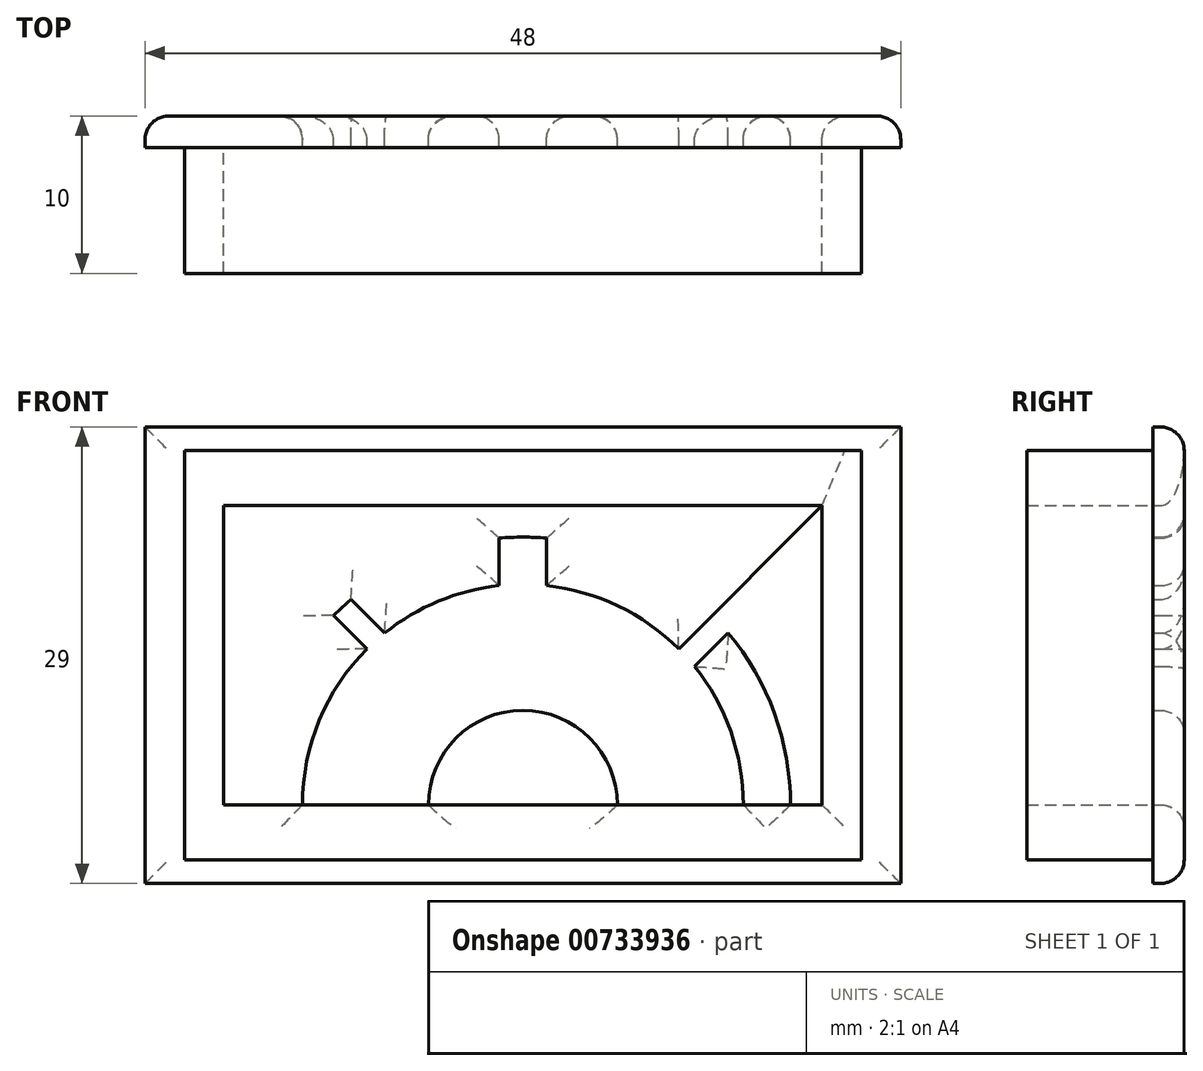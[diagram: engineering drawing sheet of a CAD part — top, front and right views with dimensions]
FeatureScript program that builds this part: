
annotation { "Feature Type Name" : "Feature", "Feature Type Description" : "" }
export const myFeature = defineFeature(function(context is Context, id is Id, definition is map)
    precondition{}
    {
        {
            var Q0;
            Q0=qCreatedBy(makeId("Front.planeOp"),FACE);
            var sketch = newSketch(context, id + "F0", { "sketchPlane" : qUnion([Q0])});
            skLineSegment(sketch, "E0.bottom", {"start": v(0, 0) * mm, "end": v(48, 0) * mm});
            skLineSegment(sketch, "E0.top", {"start": v(0, 29) * mm, "end": v(48, 29) * mm});
            skLineSegment(sketch, "E0.left", {"start": v(0, 0) * mm, "end": v(0, 29) * mm});
            skLineSegment(sketch, "E0.right", {"start": v(48, 0) * mm, "end": v(48, 29) * mm});
            skLineSegment(sketch, "E1.bottom", {"start": v(5, 24) * mm, "end": v(43, 24) * mm});
            skLineSegment(sketch, "E1.top", {"start": v(5, 5) * mm, "end": v(43, 5) * mm});
            skLineSegment(sketch, "E1.left", {"start": v(5, 24) * mm, "end": v(5, 5) * mm});
            skLineSegment(sketch, "E1.right", {"start": v(43, 24) * mm, "end": v(43, 5) * mm});
            skLineSegment(sketch, "E2.bottom", {"start": v(2.5, 27.5) * mm, "end": v(45.5, 27.5) * mm});
            skLineSegment(sketch, "E2.top", {"start": v(2.5, 1.5) * mm, "end": v(45.5, 1.5) * mm});
            skLineSegment(sketch, "E2.left", {"start": v(2.5, 27.5) * mm, "end": v(2.5, 1.5) * mm});
            skLineSegment(sketch, "E2.right", {"start": v(45.5, 27.5) * mm, "end": v(45.5, 1.5) * mm});
            skArc(sketch, "E3", {"start": v(7, 5) * mm, "mid": v(24, 22) * mm, "end": v(41, 5) * mm});
            skArc(sketch, "E4", {"start": v(10, 5) * mm, "mid": v(24, 19) * mm, "end": v(38, 5) * mm});
            skArc(sketch, "E5", {"start": v(18, 5) * mm, "mid": v(24, 11) * mm, "end": v(30, 5) * mm});
            skLineSegment(sketch, "E6", {"start": v(5, 24) * mm, "end": v(19.76, 9.24) * mm});
            skLineSegment(sketch, "E7", {"start": v(43, 24) * mm, "end": v(28.24, 9.24) * mm});
            skLineSegment(sketch, "E8", {"start": v(7.12, 24) * mm, "end": v(21.88, 9.24) * mm});
            skLineSegment(sketch, "E9", {"start": v(5, 21.88) * mm, "end": v(19.9, 6.97) * mm});
            skLineSegment(sketch, "E10", {"start": v(40.88, 24) * mm, "end": v(27.05, 10.17) * mm});
            skLineSegment(sketch, "E11", {"start": v(43, 21.88) * mm, "end": v(29.17, 8.05) * mm});
            skLineSegment(sketch, "E12", {"start": v(22.5, 24) * mm, "end": v(22.5, 10.8) * mm});
            skLineSegment(sketch, "E13", {"start": v(25.5, 24) * mm, "end": v(25.5, 10.8) * mm});
            skSolve(sketch);
        }
        {
            var Q0;
            Q0=makeQuery(id+"F0.imprint","IMPRINT",FACE,{"disambiguationData":[TD([[makeQuery(id+"F0.imprint","IMPRINT",EDGE,{"derivedFrom":sQuery(id+"F0.wireOp",EDGE,"E1.bottom")}),1.0]])]});
            extrude(context, id + "F1", {"entities" : qUnion([Q0]), "depth" : 10 * mm, "offsetDistance" : 25 * mm});
        }
        {
            var Q0;
            {var subQ0=sQuery(id+"F0.wireOp",EDGE,"E12");var subQ1=sQuery(id+"F0.wireOp",EDGE,"E1.bottom");var subQ2=makeQuery(id+"F0.imprint","INTERSECT",VERTEX,{"derivedFrom":[subQ1,subQ0]});Q0=makeQuery(id+"F0.imprint","IMPRINT",FACE,{"disambiguationData":[TD([[makeQuery(id+"F0.imprint","IMPRINT",EDGE,{"disambiguationData":[TD([[subQ2,-1.0]])],"derivedFrom":subQ1}),-1.0]])]});}
            var Q1;
            {var subQ3=sQuery(id+"F0.wireOp",EDGE,"E10");var subQ5=sQuery(id+"F0.wireOp",EDGE,"E3");var subQ6=makeQuery(id+"F0.imprint","INTERSECT",VERTEX,{"derivedFrom":[subQ5,subQ3]});Q1=makeQuery(id+"F0.imprint","IMPRINT",FACE,{"disambiguationData":[TD([[makeQuery(id+"F0.imprint","IMPRINT",EDGE,{"disambiguationData":[TD([[subQ6,-1.0]])],"derivedFrom":subQ5}),1.0]])]});}
            var Q2;
            Q2=makeQuery(id+"F0.imprint","IMPRINT",FACE,{"disambiguationData":[TD([[makeQuery(id+"F0.imprint","IMPRINT",EDGE,{"derivedFrom":sQuery(id+"F0.wireOp",EDGE,"E0.bottom")}),1.0]])]});
            var Q3;
            {var subQ0=sQuery(id+"F0.wireOp",EDGE,"E3");var subQ1=sQuery(id+"F0.wireOp",EDGE,"E1.top");var subQ2=makeQuery(id+"F0.imprint","INTERSECT",VERTEX,{"disambiguationData":[OD(0.0)],"derivedFrom":[subQ1,subQ0]});Q3=makeQuery(id+"F0.imprint","IMPRINT",FACE,{"disambiguationData":[TD([[makeQuery(id+"F0.imprint","IMPRINT",EDGE,{"disambiguationData":[TD([[subQ2,-1.0]])],"derivedFrom":subQ1}),1.0]])]});}
            var Q4;
            {var subQ0=sQuery(id+"F0.wireOp",EDGE,"E3");var subQ1=sQuery(id+"F0.wireOp",EDGE,"E1.top");var subQ2=makeQuery(id+"F0.imprint","INTERSECT",VERTEX,{"disambiguationData":[OD(1.0)],"derivedFrom":[subQ1,subQ0]});Q4=makeQuery(id+"F0.imprint","IMPRINT",FACE,{"disambiguationData":[TD([[makeQuery(id+"F0.imprint","IMPRINT",EDGE,{"disambiguationData":[TD([[subQ2,1.0]])],"derivedFrom":subQ1}),1.0]])]});}
            var Q5;
            {var subQ0=sQuery(id+"F0.wireOp",EDGE,"E9");var subQ1=sQuery(id+"F0.wireOp",EDGE,"E3");var subQ2=makeQuery(id+"F0.imprint","INTERSECT",VERTEX,{"derivedFrom":[subQ1,subQ0]});Q5=makeQuery(id+"F0.imprint","IMPRINT",FACE,{"disambiguationData":[TD([[makeQuery(id+"F0.imprint","IMPRINT",EDGE,{"disambiguationData":[TD([[subQ2,-1.0]])],"derivedFrom":subQ1}),-1.0]])]});}
            var Q6;
            {var subQ0=sQuery(id+"F0.wireOp",EDGE,"E6");var subQ1=sQuery(id+"F0.wireOp",EDGE,"E3");var subQ2=makeQuery(id+"F0.imprint","INTERSECT",VERTEX,{"derivedFrom":[subQ1,subQ0]});Q6=makeQuery(id+"F0.imprint","IMPRINT",FACE,{"disambiguationData":[TD([[makeQuery(id+"F0.imprint","IMPRINT",EDGE,{"disambiguationData":[TD([[subQ2,-1.0]])],"derivedFrom":subQ1}),-1.0]])]});}
            var Q7;
            {var subQ0=sQuery(id+"F0.wireOp",EDGE,"E8");var subQ1=sQuery(id+"F0.wireOp",EDGE,"E3");var subQ2=makeQuery(id+"F0.imprint","INTERSECT",VERTEX,{"derivedFrom":[subQ1,subQ0]});Q7=makeQuery(id+"F0.imprint","IMPRINT",FACE,{"disambiguationData":[TD([[makeQuery(id+"F0.imprint","IMPRINT",EDGE,{"disambiguationData":[TD([[subQ2,-1.0]])],"derivedFrom":subQ1}),-1.0]])]});}
            var Q8;
            {var subQ0=sQuery(id+"F0.wireOp",EDGE,"E12");var subQ1=sQuery(id+"F0.wireOp",EDGE,"E3");var subQ2=makeQuery(id+"F0.imprint","INTERSECT",VERTEX,{"derivedFrom":[subQ1,subQ0]});Q8=makeQuery(id+"F0.imprint","IMPRINT",FACE,{"disambiguationData":[TD([[makeQuery(id+"F0.imprint","IMPRINT",EDGE,{"disambiguationData":[TD([[subQ2,-1.0]])],"derivedFrom":subQ1}),-1.0]])]});}
            var Q9;
            {var subQ0=sQuery(id+"F0.wireOp",EDGE,"E13");var subQ1=sQuery(id+"F0.wireOp",EDGE,"E3");var subQ2=makeQuery(id+"F0.imprint","INTERSECT",VERTEX,{"derivedFrom":[subQ1,subQ0]});Q9=makeQuery(id+"F0.imprint","IMPRINT",FACE,{"disambiguationData":[TD([[makeQuery(id+"F0.imprint","IMPRINT",EDGE,{"disambiguationData":[TD([[subQ2,-1.0]])],"derivedFrom":subQ1}),-1.0]])]});}
            var Q10;
            {var subQ0=sQuery(id+"F0.wireOp",EDGE,"E10");var subQ1=sQuery(id+"F0.wireOp",EDGE,"E3");var subQ2=makeQuery(id+"F0.imprint","INTERSECT",VERTEX,{"derivedFrom":[subQ1,subQ0]});Q10=makeQuery(id+"F0.imprint","IMPRINT",FACE,{"disambiguationData":[TD([[makeQuery(id+"F0.imprint","IMPRINT",EDGE,{"disambiguationData":[TD([[subQ2,-1.0]])],"derivedFrom":subQ1}),-1.0]])]});}
            var Q11;
            {var subQ0=sQuery(id+"F0.wireOp",EDGE,"E7");var subQ1=sQuery(id+"F0.wireOp",EDGE,"E3");var subQ2=makeQuery(id+"F0.imprint","INTERSECT",VERTEX,{"derivedFrom":[subQ1,subQ0]});Q11=makeQuery(id+"F0.imprint","IMPRINT",FACE,{"disambiguationData":[TD([[makeQuery(id+"F0.imprint","IMPRINT",EDGE,{"disambiguationData":[TD([[subQ2,-1.0]])],"derivedFrom":subQ1}),-1.0]])]});}
            var Q12;
            Q12=makeQuery(id+"F0.imprint","IMPRINT",FACE,{"disambiguationData":[TD([[makeQuery(id+"F0.imprint","IMPRINT",EDGE,{"derivedFrom":sQuery(id+"F0.wireOp",EDGE,"E2.bottom")}),-1.0]])]});
            var Q13;
            {var subQ0=sQuery(id+"F0.wireOp",EDGE,"E6");var subQ5=sQuery(id+"F0.wireOp",EDGE,"E3");var subQ6=makeQuery(id+"F0.imprint","INTERSECT",VERTEX,{"derivedFrom":[subQ5,subQ0]});Q13=makeQuery(id+"F0.imprint","IMPRINT",FACE,{"disambiguationData":[TD([[makeQuery(id+"F0.imprint","IMPRINT",EDGE,{"disambiguationData":[TD([[subQ6,-1.0]])],"derivedFrom":subQ5}),1.0]])]});}
            var Q14;
            {var subQ3=sQuery(id+"F0.wireOp",EDGE,"E9");var subQ5=sQuery(id+"F0.wireOp",EDGE,"E3");var subQ7=makeQuery(id+"F0.imprint","INTERSECT",VERTEX,{"derivedFrom":[subQ5,subQ3]});Q14=makeQuery(id+"F0.imprint","IMPRINT",FACE,{"disambiguationData":[TD([[makeQuery(id+"F0.imprint","IMPRINT",EDGE,{"disambiguationData":[TD([[subQ7,-1.0]])],"derivedFrom":subQ5}),1.0]])]});}
            var Q15;
            {var subQ0=sQuery(id+"F0.wireOp",EDGE,"E6");var subQ1=sQuery(id+"F0.wireOp",EDGE,"E4");var subQ2=makeQuery(id+"F0.imprint","INTERSECT",VERTEX,{"derivedFrom":[subQ1,subQ0]});Q15=makeQuery(id+"F0.imprint","IMPRINT",FACE,{"disambiguationData":[TD([[makeQuery(id+"F0.imprint","IMPRINT",EDGE,{"disambiguationData":[TD([[subQ2,-1.0]])],"derivedFrom":subQ1}),-1.0]])]});}
            var Q16;
            {var subQ0=sQuery(id+"F0.wireOp",EDGE,"E9");var subQ1=sQuery(id+"F0.wireOp",EDGE,"E4");var subQ2=makeQuery(id+"F0.imprint","INTERSECT",VERTEX,{"derivedFrom":[subQ1,subQ0]});Q16=makeQuery(id+"F0.imprint","IMPRINT",FACE,{"disambiguationData":[TD([[makeQuery(id+"F0.imprint","IMPRINT",EDGE,{"disambiguationData":[TD([[subQ2,-1.0]])],"derivedFrom":subQ1}),-1.0]])]});}
            var Q17;
            {var subQ0=sQuery(id+"F0.wireOp",EDGE,"E12");var subQ1=sQuery(id+"F0.wireOp",EDGE,"E4");var subQ2=makeQuery(id+"F0.imprint","INTERSECT",VERTEX,{"derivedFrom":[subQ1,subQ0]});Q17=makeQuery(id+"F0.imprint","IMPRINT",FACE,{"disambiguationData":[TD([[makeQuery(id+"F0.imprint","IMPRINT",EDGE,{"disambiguationData":[TD([[subQ2,-1.0]])],"derivedFrom":subQ1}),-1.0]])]});}
            var Q18;
            {var subQ0=sQuery(id+"F0.wireOp",EDGE,"E10");var subQ1=sQuery(id+"F0.wireOp",EDGE,"E4");var subQ2=makeQuery(id+"F0.imprint","INTERSECT",VERTEX,{"derivedFrom":[subQ1,subQ0]});Q18=makeQuery(id+"F0.imprint","IMPRINT",FACE,{"disambiguationData":[TD([[makeQuery(id+"F0.imprint","IMPRINT",EDGE,{"disambiguationData":[TD([[subQ2,-1.0]])],"derivedFrom":subQ1}),-1.0]])]});}
            var Q19;
            {var subQ0=sQuery(id+"F0.wireOp",EDGE,"E7");var subQ1=sQuery(id+"F0.wireOp",EDGE,"E4");var subQ2=makeQuery(id+"F0.imprint","INTERSECT",VERTEX,{"derivedFrom":[subQ1,subQ0]});Q19=makeQuery(id+"F0.imprint","IMPRINT",FACE,{"disambiguationData":[TD([[makeQuery(id+"F0.imprint","IMPRINT",EDGE,{"disambiguationData":[TD([[subQ2,-1.0]])],"derivedFrom":subQ1}),-1.0]])]});}
            var Q20;
            {var subQ0=sQuery(id+"F0.wireOp",EDGE,"E7");var subQ5=sQuery(id+"F0.wireOp",EDGE,"E3");var subQ6=makeQuery(id+"F0.imprint","INTERSECT",VERTEX,{"derivedFrom":[subQ5,subQ0]});Q20=makeQuery(id+"F0.imprint","IMPRINT",FACE,{"disambiguationData":[TD([[makeQuery(id+"F0.imprint","IMPRINT",EDGE,{"disambiguationData":[TD([[subQ6,-1.0]])],"derivedFrom":subQ5}),1.0]])]});}
            var Q21;
            {var subQ0=sQuery(id+"F0.wireOp",EDGE,"E5");var subQ4=sQuery(id+"F0.wireOp",EDGE,"E1.top");var subQ5=makeQuery(id+"F0.imprint","INTERSECT",VERTEX,{"disambiguationData":[OD(0.0)],"derivedFrom":[subQ4,subQ0]});Q21=makeQuery(id+"F0.imprint","IMPRINT",FACE,{"disambiguationData":[TD([[makeQuery(id+"F0.imprint","IMPRINT",EDGE,{"disambiguationData":[TD([[subQ5,-1.0]])],"derivedFrom":subQ4}),1.0]])]});}
            extrude(context, id + "F2", {"entities" : qUnion([Q0, Q1, Q2, Q3, Q4, Q5, Q6, Q7, Q8, Q9, Q10, Q11, Q12, Q13, Q14, Q15, Q16, Q17, Q18, Q19, Q20, Q21]), "operationType" : NewBodyOperationType.ADD, "depth" : 2 * mm, "offsetDistance" : 25 * mm});
        }
        {
            var Q0;
            {var subQ0=sQuery(id+"F0.wireOp",EDGE,"E11");Q0=makeQuery(id+"F2.opExtrude","CAP_EDGE",EDGE,{"disambiguationData":[OSD([subQ0]),TDD([makeQuery(id+"F0.imprint","IMPRINT",EDGE,{"disambiguationData":[TD([[makeQuery(id+"F0.imprint","INTERSECT",VERTEX,{"derivedFrom":[sQuery(id+"F0.wireOp",EDGE,"E1.right"),subQ0]}),-1.0]])],"derivedFrom":subQ0})])],"isStart":true});}
            var Q1;
            Q1=makeQuery(id+"F1.opExtrude","CAP_EDGE",EDGE,{"disambiguationData":[OSD([sQuery(id+"F0.wireOp",EDGE,"E1.right")])],"isStart":true});
            var Q2;
            {var subQ2=sQuery(id+"F0.wireOp",EDGE,"E1.right");var subQ4=sQuery(id+"F0.wireOp",EDGE,"E1.top");Q2=makeQuery(id+"F2.boolean.opBoolean","SPLIT",EDGE,{"disambiguationData":[TD([makeQuery(id+"F1.opExtrude","SWEPT_FACE",FACE,{"disambiguationData":[OSD([subQ2])]})])],"derivedFrom":makeQuery(id+"F1.opExtrude","CAP_EDGE",EDGE,{"disambiguationData":[OSD([subQ4])],"isStart":true})});}
            var Q3;
            {var subQ0=sQuery(id+"F0.wireOp",EDGE,"E3");Q3=makeQuery(id+"F2.opExtrude","CAP_EDGE",EDGE,{"disambiguationData":[OSD([subQ0]),TDD([makeQuery(id+"F0.imprint","IMPRINT",EDGE,{"disambiguationData":[TD([[makeQuery(id+"F0.imprint","INTERSECT",VERTEX,{"disambiguationData":[OD(1.0)],"derivedFrom":[sQuery(id+"F0.wireOp",EDGE,"E1.top"),subQ0]}),1.0]])],"derivedFrom":subQ0})])],"isStart":true});}
            var Q4;
            {var subQ0=sQuery(id+"F0.wireOp",EDGE,"E10");Q4=makeQuery(id+"F2.opExtrude","CAP_EDGE",EDGE,{"disambiguationData":[OSD([subQ0]),TDD([makeQuery(id+"F0.imprint","IMPRINT",EDGE,{"disambiguationData":[TD([[makeQuery(id+"F0.imprint","INTERSECT",VERTEX,{"derivedFrom":[sQuery(id+"F0.wireOp",EDGE,"E1.bottom"),subQ0]}),-1.0]])],"derivedFrom":subQ0})])],"isStart":true});}
            var Q5;
            {var subQ1=sQuery(id+"F0.wireOp",EDGE,"E10");var subQ6=sQuery(id+"F0.wireOp",EDGE,"E1.bottom");Q5=makeQuery(id+"F2.boolean.opBoolean","SPLIT",EDGE,{"disambiguationData":[TD([makeQuery(id+"F2.opExtrude","SWEPT_FACE",FACE,{"disambiguationData":[OSD([subQ1]),TDD([makeQuery(id+"F0.imprint","IMPRINT",EDGE,{"disambiguationData":[TD([[makeQuery(id+"F0.imprint","INTERSECT",VERTEX,{"derivedFrom":[subQ6,subQ1]}),-1.0]])],"derivedFrom":subQ1})])]})])],"derivedFrom":makeQuery(id+"F1.opExtrude","CAP_EDGE",EDGE,{"disambiguationData":[OSD([subQ6])],"isStart":true})});}
            var Q6;
            {var subQ0=sQuery(id+"F0.wireOp",EDGE,"E1.right");var subQ1=sQuery(id+"F0.wireOp",EDGE,"E1.left");var subQ2=sQuery(id+"F0.wireOp",EDGE,"E1.top");var subQ3=sQuery(id+"F0.wireOp",EDGE,"E1.bottom");Q6=makeQuery(id+"F2.boolean.opBoolean","MERGE",FACE,{"derivedFrom":[makeQuery(id+"F1.opExtrude","CAP_FACE",FACE,{"disambiguationData":[OSD([subQ3,subQ2,subQ1,subQ0,sQuery(id+"F0.wireOp",EDGE,"E2.bottom"),sQuery(id+"F0.wireOp",EDGE,"E2.top"),sQuery(id+"F0.wireOp",EDGE,"E2.left"),sQuery(id+"F0.wireOp",EDGE,"E2.right")])],"isStart":true}),makeQuery(id+"F2.opExtrude","CAP_FACE",FACE,{"disambiguationData":[OSD([sQuery(id+"F0.wireOp",EDGE,"E0.bottom"),sQuery(id+"F0.wireOp",EDGE,"E0.top"),sQuery(id+"F0.wireOp",EDGE,"E0.left"),sQuery(id+"F0.wireOp",EDGE,"E0.right"),subQ3,subQ2,subQ1,subQ0,sQuery(id+"F0.wireOp",EDGE,"E3"),sQuery(id+"F0.wireOp",EDGE,"E4"),sQuery(id+"F0.wireOp",EDGE,"E5"),sQuery(id+"F0.wireOp",EDGE,"E8"),sQuery(id+"F0.wireOp",EDGE,"E9"),sQuery(id+"F0.wireOp",EDGE,"E10"),sQuery(id+"F0.wireOp",EDGE,"E11"),sQuery(id+"F0.wireOp",EDGE,"E12"),sQuery(id+"F0.wireOp",EDGE,"E13")])],"isStart":true})]});}
            fillet(context, id + "F3", {"entities" : qUnion([Q0, Q1, Q2, Q3, Q4, Q5, Q6]), "radius" : 1.5 * mm, "tangentPropagation" : true, "allowEdgeOverflow" : false});
        }
    });
